# Revit family: Keilhauer_Pact_Bench_Screen_77301
name_source: partatom
category: Furniture
revit_build: Autodesk Revit 2017 (Build: 20160225_1515(x64)
units: mm (PartAtom-declared; Revit-internal decimal feet)

## family parameters
Always vertical = Yes
Cut with Voids When Loaded = No
OmniClass Number = 23.40.70.14.64.11
OmniClass Title = Office Furniture
Room Calculation Point = No
Shared = No
Work Plane-Based = No

## types (12) — shared parameters
Assembly Code = E2020200
Catalog = Pact
Manufacturer = Keilhauer, Corp.
Product Documentation Link = http://www.keilhauer.com
URL = http://www.keilhauer.com

## per-type parameters (varying)
| type | Config | Description | Model | Size |
| 84" bench with RAF arm and privacy screen | 2 | Pact 84" bench with RAF arm and privacy screen | 77333 | 4 |
| 72" bench with RAF arm and privacy screen | 2 | Pact 72" bench with RAF arm and privacy screen | 77323 | 3 |
| 57" bench with RAF arm and privacy screen | 2 | Pact 57" bench with RAF arm and privacy screen | 77313 | 2 |
| 32" bench with RAF arm and privacy screen | 2 | Pact 32" bench with RAF arm and privacy screen | 77303 | 1 |
| 84" bench with LAF arm and privacy screen | 1 | Pact 84" bench with LAF arm and privacy screen | 77332 | 4 |
| 72" bench with LAF arm and privacy screen | 1 | Pact 72" bench with LAF arm and privacy screen | 77322 | 3 |
| 57" bench with LAF arm and privacy screen | 1 | Pact 57" bench with LAF arm and privacy screen | 77312 | 2 |
| 32" bench with LAF arm and privacy screen | 1 | Pact 32" bench with LAF arm and privacy screen | 77302 | 1 |
| 57" benches with privacy screen | 4 | Pact 57" benches with privacy screen | 77311 | 2 |
| 32" benches with privacy screen | 4 | Pact 32" benches with privacy screen | 77301 | 1 |
| 57" bench with privacy screen | 3 | Pact 57" bench with privacy screen | 77310 | 2 |
| 32" bench with privacy screen | 4 | Pact 32" bench with privacy screen | 77300 | 1 |

## geometry (parser evidence)
native form markers: Sweep x7
no freeform markers — native parametric forms only
